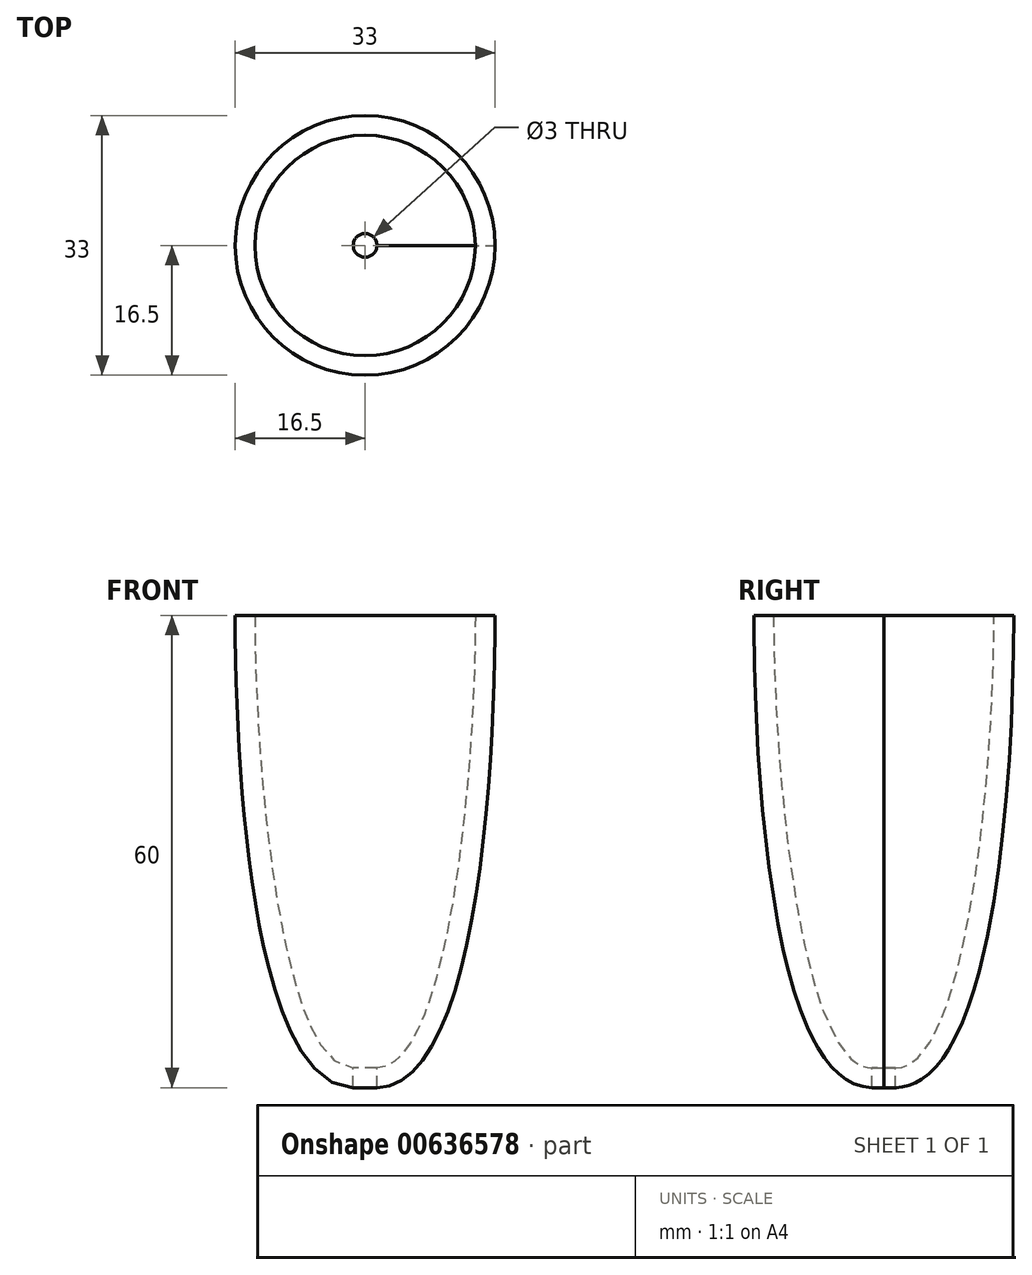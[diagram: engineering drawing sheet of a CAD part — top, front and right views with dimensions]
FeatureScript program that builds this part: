
annotation { "Feature Type Name" : "Feature", "Feature Type Description" : "" }
export const myFeature = defineFeature(function(context is Context, id is Id, definition is map)
    precondition{}
    {
        {
            var Q0;
            Q0=qCreatedBy(makeId("Front.planeOp"),FACE);
            var sketch = newSketch(context, id + "F0", { "sketchPlane" : qUnion([Q0])});
            skFitSpline(sketch, "E0", {"points": [v(-1.5, -52.8) * mm, v(-16.5, 7.2) * mm], "startDerivative": vector(-38.68, 0.79) * mm, "endDerivative": vector(0, 57.92) * mm});
            skLineSegment(sketch, "E1", {"start": v(-16.5, 7.2) * mm, "end": v(-14, 7.2) * mm});
            skLineSegment(sketch, "E2", {"start": v(-1.5, -52.8) * mm, "end": v(-1.5, -50.3) * mm});
            skFitSpline(sketch, "E3", {"points": [v(-14, 7.2) * mm, v(-1.5, -50.3) * mm], "startDerivative": vector(0, -57.92) * mm, "endDerivative": vector(27.6, -0.2) * mm});
            skLineSegment(sketch, "E4", {"start": v(0, 9.04) * mm, "end": v(0, -42.06) * mm, "construction": true});
            skSolve(sketch);
        }
        {
            var Q0;
            Q0 = qSketchRegion(id + "F0", true);
            var Q1;
            Q1=sQuery(id+"F0.wireOp",EDGE,"E4");
            revolve(context, id + "F1", {"entities" : qUnion([Q0]), "axis" : qUnion([Q1]), "revolveType" : RevolveType.FULL});
        }
    });
